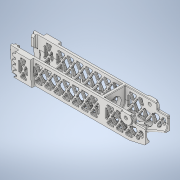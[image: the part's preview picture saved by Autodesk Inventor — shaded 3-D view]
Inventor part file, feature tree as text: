
AUTODESK INVENTOR PART (.ipt)
format: ipt  version: 2021 (Build 250183000, 183)  size: 6,170,624 bytes
history: native  units: mm
features: sketch x27, extrude x27, projected_geometry x25, fillet x13, other x5, plane x4, hole x2, mirror x2, chamfer x2
ambient origin geometry x8: Origin, YZ Plane, XZ Plane, XY Plane, X Axis, Y Axis, Z Axis, Center Point
bodies: Solid1 (feature_tree)
feature tree (107):
  sketch  "Sketch1"  dims[d0=84.0mm d1=20.0mm]
  extrude  "Extrusion1"  Depth=20.0mm
  extrude  "Extrusion2"  Depth=22.6mm TaperAngle=0.0deg
  hole  "Hole1"  [1 undecoded]
  other  "PivotPointSketch"
  extrude  "Extrusion3"  Depth=2.0mm TaperAngle=0.0deg
  extrude  "PivotPointFace"  Depth=65.0mm
  sketch  "Sketch37"  dims[d198=2.0mm d200=2.0mm]
  extrude  "Extrusion4"  Depth=2.6mm TaperAngle=0.0deg
  sketch  "Sketch6"  dims[d8=14.0mm d9=6.0mm d10=4.0mm d11=2.0mm d12=90.0deg d13=8.0mm d14=20.594885mm d17=2.0mm d18=0.0mm]
  hole  "PivotHole"  [1 undecoded]
  extrude  "Extrusion5"  Depth=4.0mm
  extrude  "Extrusion6"  Depth=45.0mm
  extrude  "Extrusion8"  Depth=2.6mm TaperAngle=0.0deg
  extrude  "Extrusion9"  Depth=1.5mm
  extrude  "Extrusion10"  Depth=2.6mm TaperAngle=0.0deg
  extrude  "Extrusion11"  Depth=11.8mm
  fillet  "Fillet1"  Radius=10.0mm
  sketch  "Sketch16"  dims[d60=4.0mm d61=1.5mm]
  plane  "Work Plane4"
  extrude  "Extrusion13"  Depth=0.5mm TaperAngle=0.0deg
  other  "CentreLine"
  plane  "Work Plane5"
  extrude  "Extrusion14"  Depth=0.5mm
  extrude  "Extrusion15"  TaperAngle=45.0deg  [1 undecoded]
  mirror  "Mirror4"
  fillet  "Fillet2"  Radius=3.0mm
  extrude  "Extrusion17"  Depth=8.0mm
  fillet  "Fillet3"  [1 undecoded]
  fillet  "Fillet4"  [1 undecoded]
  plane  "Work Plane3"
  extrude  "Extrusion18"  Depth=0.5mm
  sketch  "Sketch25"  dims[d87=5.5mm d91=8.0mm d95=0.0mm d96=180.0deg]
  mirror  "Mirror3"
  extrude  "Extrusion31"  Depth=3.441mm
  extrude  "Extrusion23"  Depth=1.0mm
  extrude  "Extrusion19"  Depth=8.0mm
  fillet  "Fillet5"  Radius=1.0mm
  fillet  "Fillet6"  Radius=1.0mm
  fillet  "Fillet7"  Radius=1.0mm
  fillet  "Fillet8"  Radius=1.0mm
  chamfer  "Chamfer1"  Distance=1.0mm Angle=45.0deg
  extrude  "Extrusion22"  Depth=3.0mm TaperAngle=90.0deg
  extrude  "Extrusion25"  TaperAngle=0.0deg  [1 undecoded]
  extrude  "Extrusion26"  Depth=2.0mm
  extrude  "Extrusion27"  Depth=1.0mm
  extrude  "Extrusion28"  TaperAngle=0.0deg  [1 undecoded]
  chamfer  "Chamfer2"  [1 undecoded]
  plane  "Work Plane6"
  extrude  "Extrusion32"  Depth=1.0mm TaperAngle=45.0deg
  fillet  "Fillet15"  Radius=2.251475mm
  fillet  "Fillet16"  Radius=0.25mm
  extrude  "Extrusion33"  Depth=2.251475mm
  fillet  "Fillet17"  Radius=0.75mm
  fillet  "Fillet18"  Radius=0.75mm
  fillet  "Fillet19"  Radius=2.6mm
  extrude  "Extrusion34"  Depth=2.6mm
  other  "Side Profile"
  other  "Top Profile"
  other  "SpringMechHolder"
  sketch  "Sketch2"  dims[d2=2.6mm d3=22.6mm d4=0.0mm]
  sketch  "Sketch4"  dims[d5=20.0mm d6=0.0mm d7=9.25mm]
  sketch  "Sketch7"  dims[d27=20.0mm d28=0.0mm d29=65.0mm]
  sketch  "Sketch8"  dims[d30=18.0mm d35=2.6mm d36=0.0mm]
  projected_geometry  "Projected Loop1"
  sketch  "Sketch12"  dims[d37=2.6mm d38=0.0mm d42=4.1mm]
  sketch  "Sketch13"  dims[d52=2.6mm d53=0.0mm d54=4.0mm]
  sketch  "Sketch14"  dims[d55=10.0mm d56=45.0mm]
  sketch  "Sketch15"  dims[d57=14.0mm d58=2.6mm d59=0.0mm]
  sketch  "Sketch17"  dims[d62=2.6mm d63=0.0mm d64=2.6mm d65=0.0mm]
  sketch  "Sketch19"  dims[d66=2.0mm d67=11.8mm d72=10.0mm d73=0.0mm]
  projected_geometry  "Projected Loop7"
  sketch  "Sketch20"  dims[d74=10.0mm d75=0.5mm d76=0.0mm]
  projected_geometry  "Projected Loop8"
  sketch  "Sketch22"  dims[d77=0.5mm d78=0.0mm d79=0.5mm]
  sketch  "Sketch24"  dims[d84=13.441mm d85=45.0deg d86=3.0mm]
  sketch  "Sketch27"  dims[d97=20.0mm d98=0.0mm d99=0.5mm]
  sketch  "Sketch28"  dims[d100=8.0mm d101=3.441mm]
  sketch  "Sketch30"  dims[d102=10.0mm d103=0.0mm d109=1.0mm]
  sketch  "Sketch31"  dims[d110=10.0mm d111=0.0mm d112=8.0mm d113=1.0mm d114=1.0mm d115=1.0mm d116=1.0mm d117=1.0mm d118=2.0mm d119=45.0deg]
  sketch  "Sketch32"  dims[d124=1.0mm d162=3.0mm d164=3.0mm d168=90.0deg]
  sketch  "Sketch33"  dims[d173=60.0deg d174=2.0mm d175=60.0deg d181=60.0deg d184=2.0mm d194=0.0mm d195=0.0mm]
  sketch  "Sketch38"  dims[d202=0.0mm d203=0.0mm d226=1.0mm]
  projected_geometry  "Projected Loop9"
  sketch  "Sketch39"  dims[d227=0.0mm d228=0.0mm d229=0.0mm d230=0.0mm d231=0.0mm d232=0.0mm]
  projected_geometry  "Projected Loop12"
  sketch  "Sketch40"  dims[d233=1.0mm d234=0.0mm d235=1.0mm d236=2.0mm d237=45.0deg d244=2.251475mm d245=0.25mm d246=2.251475mm d247=0.75mm d248=0.0mm d249=3.2mm d250=6.0mm d251=6.5mm d252=3.0mm d253=90.0deg d254=8.0mm d255=20.594885mm d256=0.75mm d257=0.0mm d261=2.6mm d262=3.0mm d263=2.6mm d264=2.6mm d267=1.0mm d269=0.5mm d270=180.0deg d275=3.0mm d276=3.0mm d277=-1.8mm d279=70.0mm d281=9.002mm d282=10.0mm d284=10.0mm d286=0.6mm d288=0.0mm d289=0.0mm d290=0.5mm d291=14.8mm d292=40.0mm d294=9.006mm d295=10.0mm d297=10.0mm d299=0.0mm d303=1.0mm d304=1.0mm d305=3.4mm d306=1.0mm d307=1.0mm d309=1.0mm d310=0.75mm d311=0.0mm d312=0.35mm d313=0.5mm d314=0.5mm d315=0.75mm d316=0.0mm d238=0.5mm d239=0.872665mm d240=0.5mm d241=0.872665mm]
  projected_geometry  "Projected Loop13"
  projected_geometry  "Projected Loop14"
  projected_geometry  "Projected Loop15"
  projected_geometry  "Projected Loop16"
  projected_geometry  "Projected Loop17"
  projected_geometry  "Projected Loop18"
  projected_geometry  "Projected Loop19"
  projected_geometry  "Projected Loop20"
  projected_geometry  "Projected Loop21"
  projected_geometry  "Projected Loop22"
  projected_geometry  "Projected Loop23"
  projected_geometry  "Projected Loop24"
  projected_geometry  "Projected Loop25"
  projected_geometry  "Projected Loop26"
  projected_geometry  "Projected Loop27"
  projected_geometry  "Projected Loop28"
  projected_geometry  "Projected Loop29"
  projected_geometry  "Project Cut Edges5"
  projected_geometry  "Project Cut Edges8"
  projected_geometry  "Project Cut Edges11"
note: 8 required parameter values undecoded (feature->parameter linkage not recoverable at this tier; creation-order binding heuristic only, values carry confidence <= 0.55)
